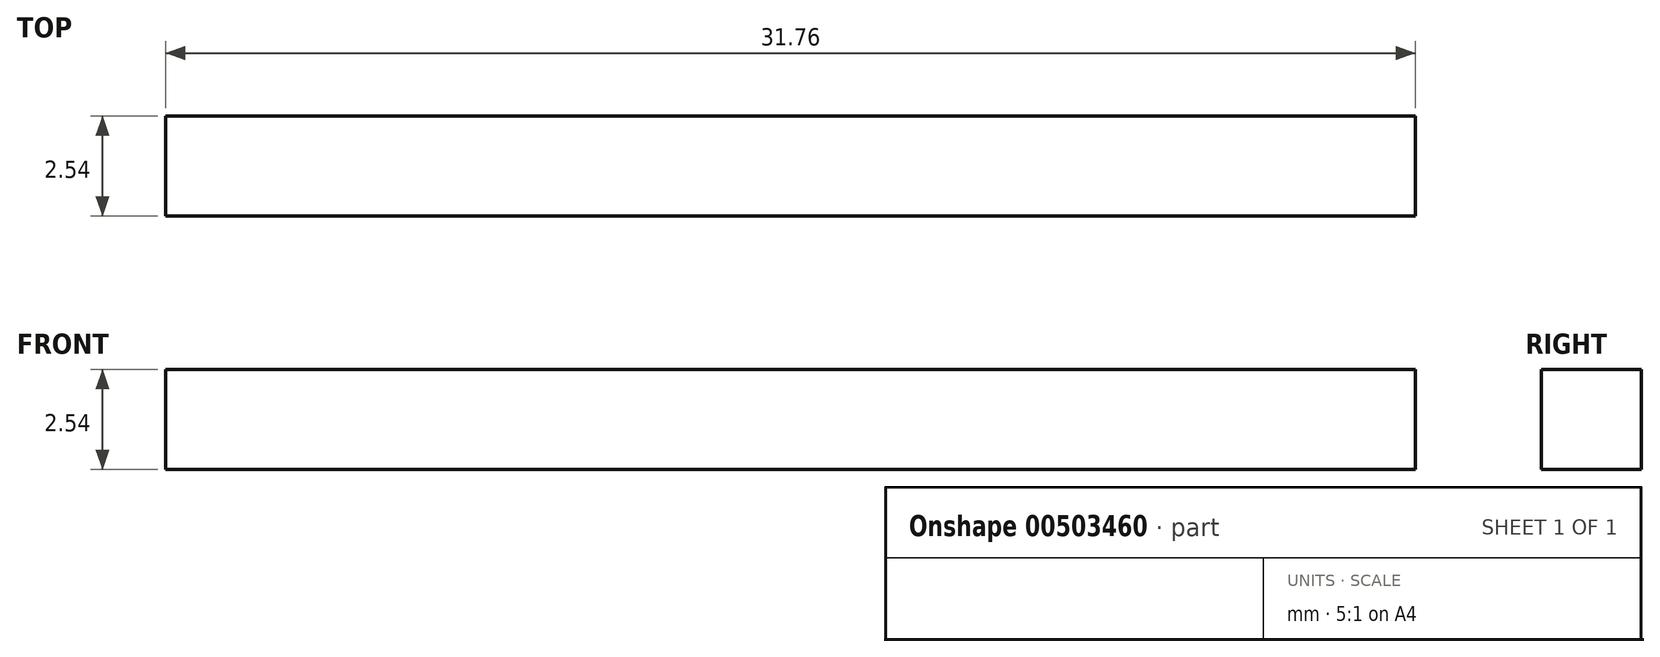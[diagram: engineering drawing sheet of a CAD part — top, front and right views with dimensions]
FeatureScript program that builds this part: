
annotation { "Feature Type Name" : "Feature", "Feature Type Description" : "" }
export const myFeature = defineFeature(function(context is Context, id is Id, definition is map)
    precondition{}
    {
        {
            var Q0;
            Q0=qCreatedBy(makeId("Front.planeOp"),FACE);
            var sketch = newSketch(context, id + "F0", { "sketchPlane" : qUnion([Q0])});
            skLineSegment(sketch, "E0", {"start": v(0, 0) * mm, "end": v(-15.87, 0) * mm});
            skLineSegment(sketch, "E1", {"start": v(-15.88, 0) * mm, "end": v(-15.88, 2.54) * mm});
            skLineSegment(sketch, "E2", {"start": v(-15.88, 2.54) * mm, "end": v(0, 2.54) * mm});
            skLineSegment(sketch, "E3.MirrorCS", {"start": v(0, 2.54) * mm, "end": v(0, 0) * mm});
            skLineSegment(sketch, "E4.MirrorCS", {"start": v(15.88, 2.54) * mm, "end": v(0, 2.54) * mm});
            skLineSegment(sketch, "E5.MirrorCS", {"start": v(15.88, 0) * mm, "end": v(15.88, 2.54) * mm});
            skLineSegment(sketch, "E6.MirrorCS", {"start": v(0, 0) * mm, "end": v(15.87, 0) * mm});
            skLineSegment(sketch, "E7", {"start": v(-17.36, -2.58) * mm, "end": v(17.36, -2.58) * mm});
            skLineSegment(sketch, "E8.MirrorCS", {"start": v(0, -2.54) * mm, "end": v(0, 0) * mm});
            skSolve(sketch);
        }
        {
            var Q0;
            Q0=makeQuery(id+"F0.imprint","IMPRINT",FACE,{"disambiguationData":[TD([[makeQuery(id+"F0.imprint","IMPRINT",EDGE,{"derivedFrom":sQuery(id+"F0.wireOp",EDGE,"E3.MirrorCS")}),1.0]])]});
            var Q1;
            Q1=makeQuery(id+"F0.imprint","IMPRINT",FACE,{"disambiguationData":[TD([[makeQuery(id+"F0.imprint","IMPRINT",EDGE,{"derivedFrom":sQuery(id+"F0.wireOp",EDGE,"E0")}),-1.0]])]});
            extrude(context, id + "F1", {"entities" : qUnion([Q0, Q1]), "depth" : 2.54 * mm, "offsetDistance" : 25.4 * mm, "symmetric" : true});
        }
    });
